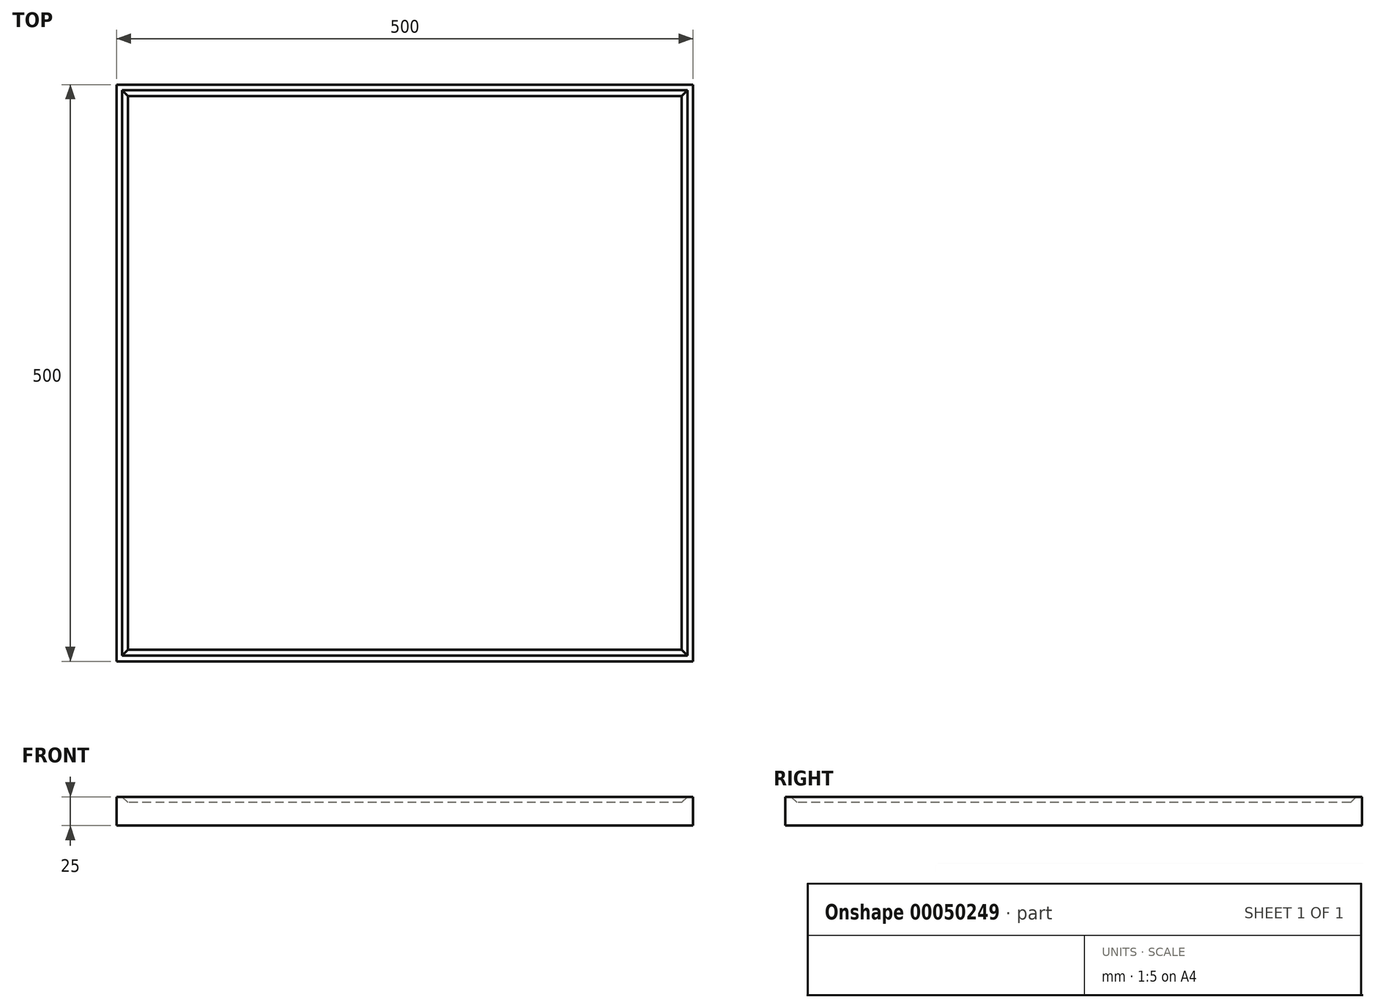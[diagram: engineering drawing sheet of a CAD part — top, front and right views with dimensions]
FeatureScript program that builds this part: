
annotation { "Feature Type Name" : "Feature", "Feature Type Description" : "" }
export const myFeature = defineFeature(function(context is Context, id is Id, definition is map)
    precondition{}
    {
        {
            var Q0;
            Q0=qCreatedBy(makeId("Top.planeOp"),FACE);
            var sketch = newSketch(context, id + "F0", { "sketchPlane" : qUnion([Q0])});
            skLineSegment(sketch, "E0.rect.bottom", {"start": v(250, -250) * mm, "end": v(-250, -250) * mm});
            skLineSegment(sketch, "E0.rect.top", {"start": v(250, 250) * mm, "end": v(-250, 250) * mm});
            skLineSegment(sketch, "E0.rect.left", {"start": v(250, -250) * mm, "end": v(250, 250) * mm});
            skLineSegment(sketch, "E0.rect.right", {"start": v(-250, -250) * mm, "end": v(-250, 250) * mm});
            skPoint(sketch, "E0.rect.middle", {"position": v(0, 0) * mm});
            skSolve(sketch);
        }
        {
            var Q0;
            Q0 = qSketchRegion(id + "F0", true);
            extrude(context, id + "F1", {"entities" : qUnion([Q0]), "depth" : 25 * mm});
        }
        {
            var Q0;
            Q0=makeQuery(id+"F1.opExtrude","CAP_FACE",FACE,{"disambiguationData":[OSD([sQuery(id+"F0.wireOp",EDGE,"E0.rect.bottom"),sQuery(id+"F0.wireOp",EDGE,"E0.rect.top"),sQuery(id+"F0.wireOp",EDGE,"E0.rect.left"),sQuery(id+"F0.wireOp",EDGE,"E0.rect.right")])],"isStart":false});
            var sketch = newSketch(context, id + "F2", { "sketchPlane" : qUnion([Q0])});
            skLineSegment(sketch, "E1.0", {"start": v(245, 245) * mm, "end": v(-245, 245) * mm});
            skLineSegment(sketch, "E1.1", {"start": v(245, -245) * mm, "end": v(245, 245) * mm});
            skLineSegment(sketch, "E1.2", {"start": v(245, -245) * mm, "end": v(-245, -245) * mm});
            skLineSegment(sketch, "E1.3", {"start": v(-245, -245) * mm, "end": v(-245, 245) * mm});
            skSolve(sketch);
        }
        {
            var Q0;
            Q0 = qSketchRegion(id + "F2", true);
            extrude(context, id + "F3", {"entities" : qUnion([Q0]), "operationType" : NewBodyOperationType.REMOVE, "oppositeDirection" : true, "depth" : 5 * mm});
        }
        {
            var Q0;
            Q0=makeQuery(id+"F3.boolean.opBoolean","COPY",FACE,{"derivedFrom":makeQuery(id+"F3.opExtrude","CAP_FACE",FACE,{"disambiguationData":[OSD([sQuery(id+"F2.wireOp",EDGE,"E1.0"),sQuery(id+"F2.wireOp",EDGE,"E1.1"),sQuery(id+"F2.wireOp",EDGE,"E1.2"),sQuery(id+"F2.wireOp",EDGE,"E1.3")])],"isStart":false})});
            chamfer(context, id + "F4", {"entities" : qUnion([Q0]), "width" : 5 * mm, "tangentPropagation" : true});
        }
    });
